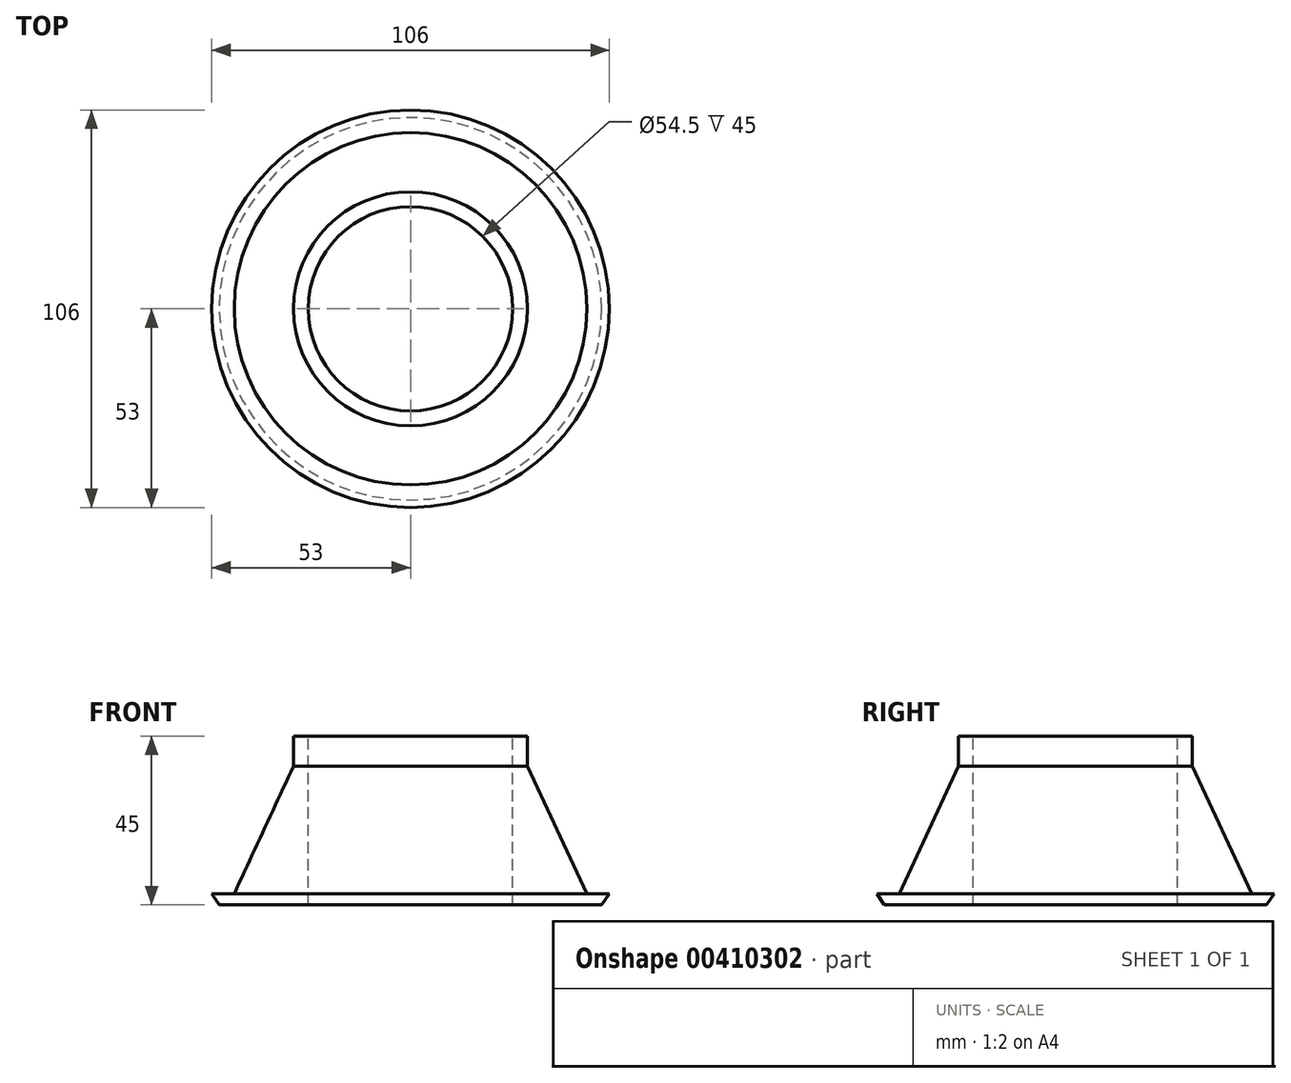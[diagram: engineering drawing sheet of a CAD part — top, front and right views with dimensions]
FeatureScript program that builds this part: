
annotation { "Feature Type Name" : "Feature", "Feature Type Description" : "" }
export const myFeature = defineFeature(function(context is Context, id is Id, definition is map)
    precondition{}
    {
        {
            var Q0;
            Q0=qCreatedBy(makeId("Front.planeOp"),FACE);
            var sketch = newSketch(context, id + "F0", { "sketchPlane" : qUnion([Q0])});
            skLineSegment(sketch, "E0", {"start": v(0, 0) * mm, "end": v(0, 45) * mm});
            skLineSegment(sketch, "E1", {"start": v(0, 45) * mm, "end": v(-31.2, 45) * mm});
            skLineSegment(sketch, "E2", {"start": v(-31.2, 45) * mm, "end": v(-31.2, 37) * mm});
            skLineSegment(sketch, "E3", {"start": v(-31.2, 37) * mm, "end": v(-47, 3) * mm});
            skLineSegment(sketch, "E4", {"start": v(-47, 3) * mm, "end": v(-53, 3) * mm});
            skLineSegment(sketch, "E5", {"start": v(-53, 3) * mm, "end": v(-51, 0) * mm});
            skLineSegment(sketch, "E6", {"start": v(-51, 0) * mm, "end": v(0, 0) * mm});
            skSolve(sketch);
        }
        {
            var Q0;
            Q0=makeQuery(id+"F0.imprint","IMPRINT",FACE,{"disambiguationData":[TD([[makeQuery(id+"F0.imprint","IMPRINT",EDGE,{"derivedFrom":sQuery(id+"F0.wireOp",EDGE,"E0")}),1.0]])]});
            var Q1;
            Q1=sQuery(id+"F0.wireOp",EDGE,"E0");
            revolve(context, id + "F1", {"entities" : qUnion([Q0]), "axis" : qUnion([Q1]), "revolveType" : RevolveType.FULL});
        }
        {
            var Q0;
            Q0=makeQuery(id+"F1.opRevolve","SWEPT_FACE",FACE,{"disambiguationData":[OSD([sQuery(id+"F0.wireOp",EDGE,"E1")])]});
            var sketch = newSketch(context, id + "F2", { "sketchPlane" : qUnion([Q0])});
            skCircle(sketch, "E7", {"center": v(0, 0) * mm, "radius": 27.25 * mm});
            skSolve(sketch);
        }
        {
            var Q0;
            Q0 = qSketchRegion(id + "F2", true);
            extrude(context, id + "F3", {"entities" : qUnion([Q0]), "operationType" : NewBodyOperationType.REMOVE, "endBound" : BoundingType.THROUGH_ALL, "oppositeDirection" : true, "depth" : 25 * mm});
        }
    });
